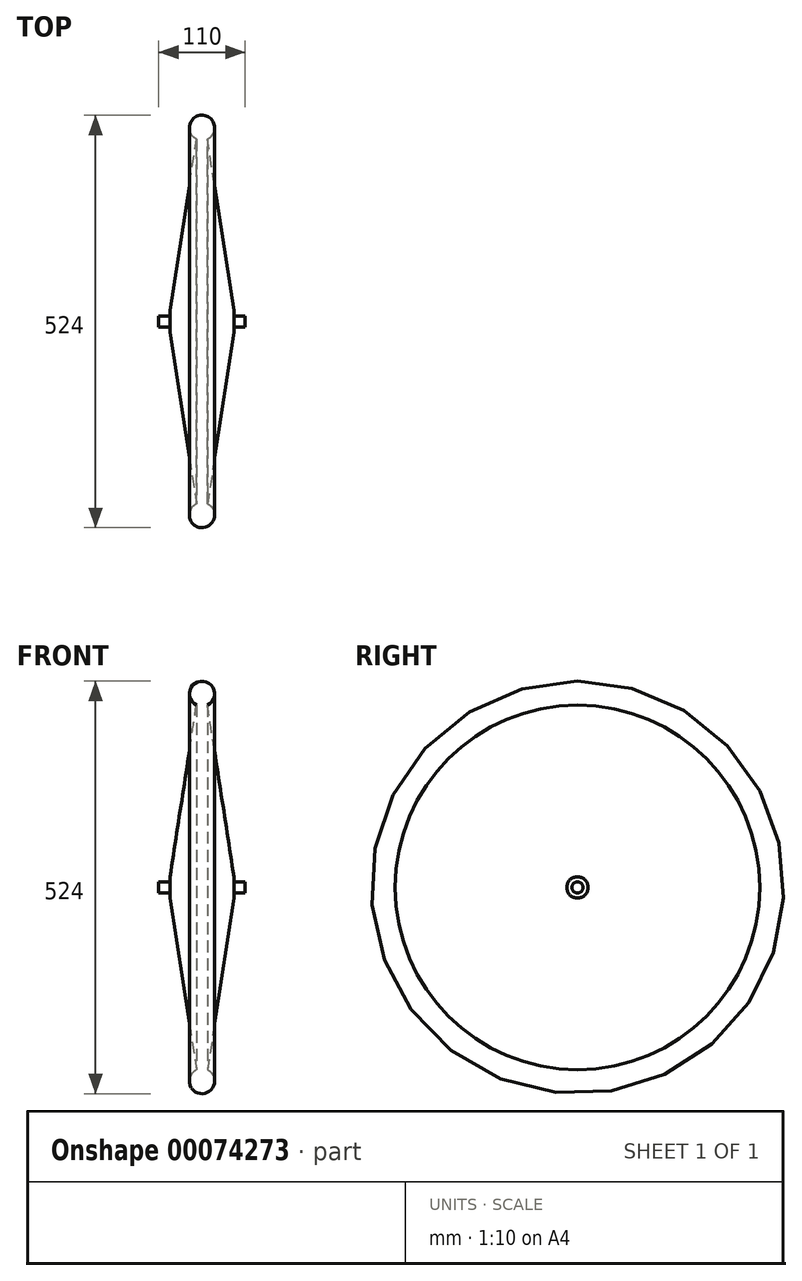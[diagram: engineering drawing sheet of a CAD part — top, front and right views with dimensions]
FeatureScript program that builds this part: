
annotation { "Feature Type Name" : "Feature", "Feature Type Description" : "" }
export const myFeature = defineFeature(function(context is Context, id is Id, definition is map)
    precondition{}
    {
        {
            var Q0;
            Q0=qCreatedBy(makeId("Top.planeOp"),FACE);
            var sketch = newSketch(context, id + "F0", { "sketchPlane" : qUnion([Q0])});
            skLineSegment(sketch, "E0.bottom", {"start": v(0, 0) * mm, "end": v(110, 0) * mm});
            skLineSegment(sketch, "E0.top", {"start": v(0, 7.12) * mm, "end": v(110, 7.12) * mm});
            skLineSegment(sketch, "E0.left", {"start": v(0, 0) * mm, "end": v(0, 7.12) * mm});
            skLineSegment(sketch, "E0.right", {"start": v(110, 0) * mm, "end": v(110, 7.12) * mm});
            skLineSegment(sketch, "E1", {"start": v(55, 0) * mm, "end": v(55, 262) * mm, "construction": true});
            skPoint(sketch, "E1.endSnap0", {"position": v(55, 7.12) * mm});
            skLineSegment(sketch, "E2", {"start": v(55, 0) * mm, "end": v(55, 262) * mm});
            skCircle(sketch, "E3", {"center": v(55, 246) * mm, "radius": 16 * mm});
            skLineSegment(sketch, "E4.rect.bottom", {"start": v(95.55, 13.59) * mm, "end": v(14.45, 13.59) * mm});
            skLineSegment(sketch, "E4.rect.left", {"start": v(95.55, 13.59) * mm, "end": v(95.55, 0) * mm});
            skLineSegment(sketch, "E4.rect.right", {"start": v(14.45, 13.59) * mm, "end": v(14.45, 0) * mm});
            skPoint(sketch, "E4.rect.middle", {"position": v(55, 0) * mm});
            skLineSegment(sketch, "E5", {"start": v(14.45, 13.59) * mm, "end": v(47.97, 231.63) * mm});
            skLineSegment(sketch, "E6.MirrorCS", {"start": v(95.55, 13.59) * mm, "end": v(62.03, 231.63) * mm});
            skSolve(sketch);
        }
        {
            var Q0;
            Q0 = qSketchRegion(id + "F0", true);
            var Q1;
            Q1=sQuery(id+"F0.wireOp",EDGE,"E0.bottom");
            revolve(context, id + "F1", {"entities" : qUnion([Q0]), "axis" : qUnion([Q1]), "revolveType" : RevolveType.FULL});
        }
    });
